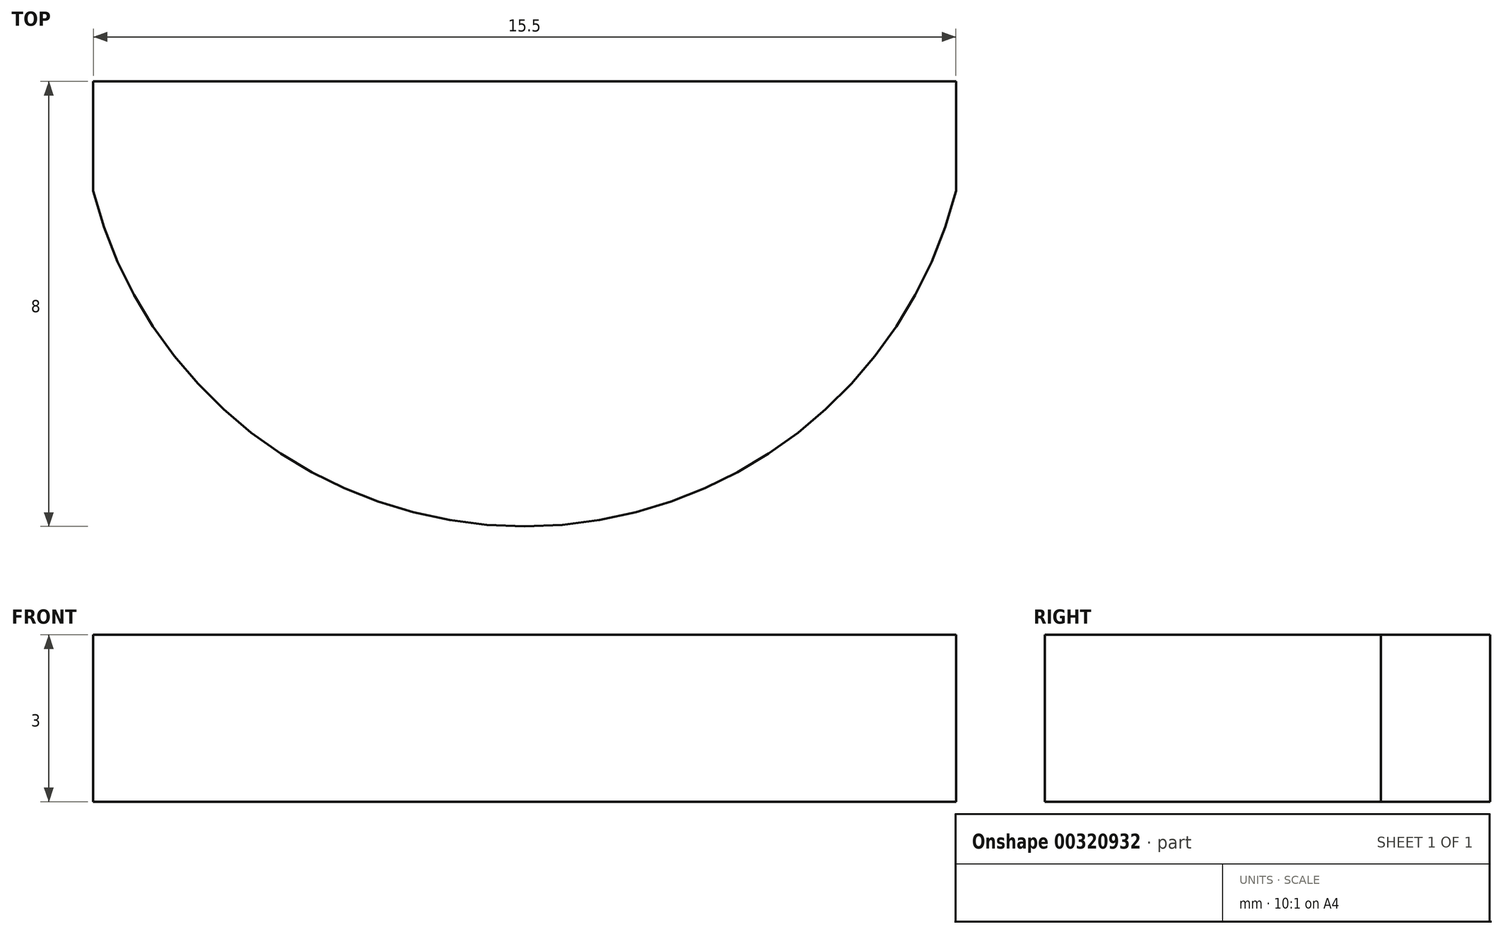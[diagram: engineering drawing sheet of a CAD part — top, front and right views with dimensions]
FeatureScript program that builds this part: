
annotation { "Feature Type Name" : "Feature", "Feature Type Description" : "" }
export const myFeature = defineFeature(function(context is Context, id is Id, definition is map)
    precondition{}
    {
        {
            var Q0;
            Q0=qCreatedBy(makeId("Top.planeOp"),FACE);
            var sketch = newSketch(context, id + "F0", { "sketchPlane" : qUnion([Q0])});
            skArc(sketch, "E0", {"start": v(-7.75, -1.97) * mm, "mid": v(0, -8) * mm, "end": v(7.75, -1.97) * mm});
            skLineSegment(sketch, "E1", {"start": v(-7.75, 0) * mm, "end": v(7.75, 0) * mm});
            skLineSegment(sketch, "E2.left", {"start": v(-7.75, -1.97) * mm, "end": v(-7.75, 0) * mm});
            skLineSegment(sketch, "E2.right", {"start": v(7.75, -1.97) * mm, "end": v(7.75, 0) * mm});
            skSolve(sketch);
        }
        {
            var Q0;
            Q0=makeQuery(id+"F0.imprint","IMPRINT",FACE,{"disambiguationData":[TD([[makeQuery(id+"F0.imprint","IMPRINT",EDGE,{"derivedFrom":sQuery(id+"F0.wireOp",EDGE,"E0")}),1.0]])]});
            extrude(context, id + "F1", {"entities" : qUnion([Q0]), "depth" : 3 * mm});
        }
    });
